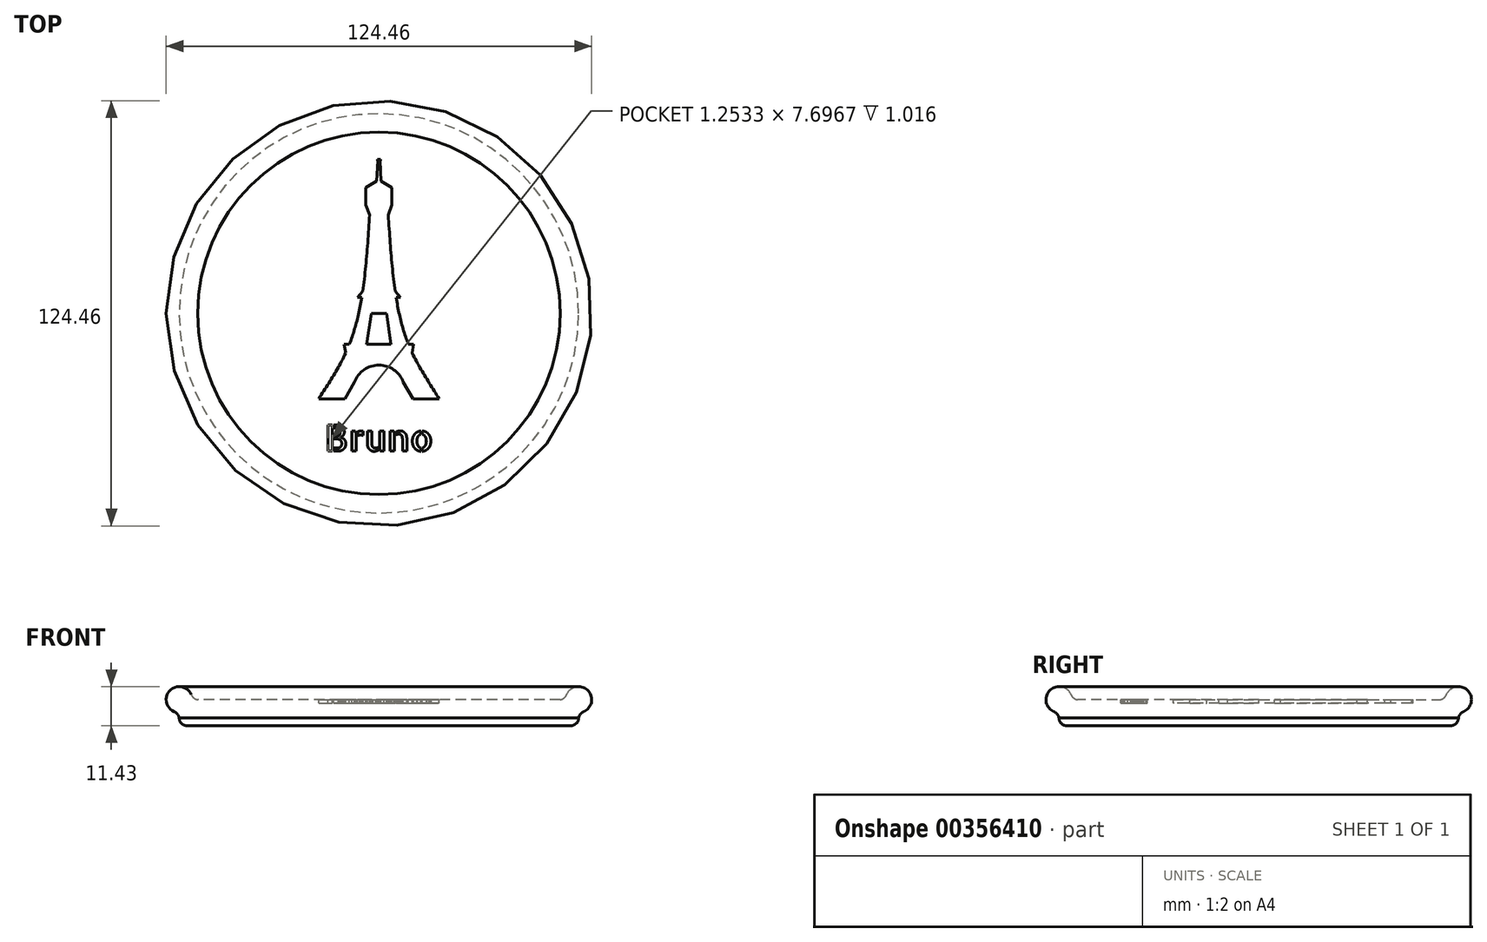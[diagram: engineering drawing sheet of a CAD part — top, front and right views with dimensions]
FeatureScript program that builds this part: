
annotation { "Feature Type Name" : "Feature", "Feature Type Description" : "" }
export const myFeature = defineFeature(function(context is Context, id is Id, definition is map)
    precondition{}
    {
        {
            var Q0;
            Q0=qCreatedBy(makeId("Top.planeOp"),FACE);
            var sketch = newSketch(context, id + "F0", { "sketchPlane" : qUnion([Q0])});
            skCircle(sketch, "E0", {"center": v(0, 0) * mm, "radius": 58.42 * mm});
            skSolve(sketch);
        }
        {
            var Q0;
            Q0=makeQuery(id+"F0.imprint","IMPRINT",FACE,{"disambiguationData":[TD([[makeQuery(id+"F0.imprint","IMPRINT",EDGE,{"derivedFrom":sQuery(id+"F0.wireOp",EDGE,"E0")}),1.0]])]});
            extrude(context, id + "F1", {"entities" : qUnion([Q0]), "depth" : 7.62 * mm, "offsetDistance" : 25.4 * mm});
        }
        {
            var Q0;
            Q0=makeQuery(id+"F1.opExtrude","CAP_FACE",FACE,{"disambiguationData":[OSD([sQuery(id+"F0.wireOp",EDGE,"E0")])],"isStart":false});
            var sketch = newSketch(context, id + "F2", { "sketchPlane" : qUnion([Q0])});
            skLineSegment(sketch, "E1", {"start": v(0, 0) * mm, "end": v(-58.42, 0) * mm});
            skSolve(sketch);
        }
        {
            var Q0;
            Q0=sQuery(id+"F2.wireOp",EDGE,"E1");
            cPlane(context, id + "F3", {"entities" : qUnion([Q0]), "cplaneType" : CPlaneType.LINE_ANGLE, "offset" : 25.4 * mm, "angle" : 0 * degree, "width" : 152.4 * mm, "height" : 152.4 * mm});
        }
        {
            var Q0;
            Q0=qCreatedBy(id+"F3.planeOp",FACE);
            var sketch = newSketch(context, id + "F4", { "sketchPlane" : qUnion([Q0])});
            skCircle(sketch, "E2", {"center": v(-58.42, 7.62) * mm, "radius": 3.81 * mm});
            skLineSegment(sketch, "E3", {"start": v(-58.42, 7.62) * mm, "end": v(-54.9, 9.08) * mm});
            skLineSegment(sketch, "E4", {"start": v(-54.9, 9.08) * mm, "end": v(-61.94, 6.16) * mm});
            skLineSegment(sketch, "E5", {"start": v(-54.9, 9.08) * mm, "end": v(-54.3, 7.62) * mm});
            skArc(sketch, "E6", {"start": v(-54.9, 9.08) * mm, "mid": v(-54.16, 8.1) * mm, "end": v(-53.03, 7.62) * mm});
            skLineSegment(sketch, "E7", {"start": v(-54.3, 7.62) * mm, "end": v(-53.03, 7.62) * mm});
            skLineSegment(sketch, "E8", {"start": v(-58.42, 7.62) * mm, "end": v(-59.88, 4.1) * mm});
            skLineSegment(sketch, "E9", {"start": v(-59.88, 4.1) * mm, "end": v(-58.42, 3.5) * mm});
            skLineSegment(sketch, "E10", {"start": v(-58.42, 3.5) * mm, "end": v(-58.42, 2.23) * mm});
            skArc(sketch, "E11", {"start": v(-58.42, 2.23) * mm, "mid": v(-58.9, 3.36) * mm, "end": v(-59.88, 4.1) * mm});
            skLineSegment(sketch, "E12", {"start": v(-58.42, 3.5) * mm, "end": v(-58.42, 3.81) * mm});
            skLineSegment(sketch, "E13", {"start": v(-54.3, 7.62) * mm, "end": v(-54.6, 7.62) * mm});
            skSolve(sketch);
        }
        {
            var Q0;
            {var subQ0=sQuery(id+"F4.wireOp",EDGE,"E4");var subQ1=sQuery(id+"F4.wireOp",EDGE,"E2");var subQ3=makeQuery(id+"F4.imprint","INTERSECT",VERTEX,{"derivedFrom":[subQ1,subQ0]});Q0=makeQuery(id+"F4.imprint","IMPRINT",FACE,{"disambiguationData":[TD([[makeQuery(id+"F4.imprint","IMPRINT",EDGE,{"disambiguationData":[TD([[subQ3,1.0]])],"derivedFrom":subQ0}),-1.0]])]});}
            var Q1;
            {var subQ3=sQuery(id+"F4.wireOp",EDGE,"E8");Q1=makeQuery(id+"F4.imprint","IMPRINT",FACE,{"disambiguationData":[TD([[makeQuery(id+"F4.imprint","IMPRINT",EDGE,{"derivedFrom":subQ3}),-1.0]])]});}
            var Q2;
            {var subQ3=sQuery(id+"F4.wireOp",EDGE,"E8");Q2=makeQuery(id+"F4.imprint","IMPRINT",FACE,{"disambiguationData":[TD([[makeQuery(id+"F4.imprint","IMPRINT",EDGE,{"derivedFrom":subQ3}),1.0]])]});}
            var Q3;
            {var subQ0=sQuery(id+"F4.wireOp",EDGE,"E5");Q3=makeQuery(id+"F4.imprint","IMPRINT",FACE,{"disambiguationData":[TD([[makeQuery(id+"F4.imprint","IMPRINT",EDGE,{"derivedFrom":subQ0}),-1.0]])]});}
            var Q4;
            Q4=makeQuery(id+"F4.imprint","IMPRINT",FACE,{"disambiguationData":[TD([[makeQuery(id+"F4.imprint","IMPRINT",EDGE,{"derivedFrom":sQuery(id+"F4.wireOp",EDGE,"E5")}),1.0]])]});
            var Q5;
            Q5=makeQuery(id+"F4.imprint","IMPRINT",FACE,{"disambiguationData":[TD([[makeQuery(id+"F4.imprint","IMPRINT",EDGE,{"derivedFrom":sQuery(id+"F4.wireOp",EDGE,"E9")}),-1.0]])]});
            var Q6;
            {var subQ0=sQuery(id+"F4.wireOp",EDGE,"E9");Q6=makeQuery(id+"F4.imprint","IMPRINT",FACE,{"disambiguationData":[TD([[makeQuery(id+"F4.imprint","IMPRINT",EDGE,{"derivedFrom":subQ0}),1.0]])]});}
            var Q7;
            Q7=makeQuery(id+"F1.opExtrude","CAP_EDGE",EDGE,{"disambiguationData":[OSD([sQuery(id+"F0.wireOp",EDGE,"E0")])],"isStart":false});
            revolve(context, id + "F5", {"operationType" : NewBodyOperationType.ADD, "surfaceOperationType" : NewSurfaceOperationType.NEW, "entities" : qUnion([Q0, Q1, Q2, Q3, Q4, Q5, Q6]), "axis" : qUnion([Q7]), "revolveType" : RevolveType.FULL});
        }
        {
            var Q0;
            Q0=makeQuery(id+"F1.opExtrude","CAP_EDGE",EDGE,{"disambiguationData":[OSD([sQuery(id+"F0.wireOp",EDGE,"E0")])],"isStart":true});
            fillet(context, id + "F6", {"entities" : qUnion([Q0]), "radius" : 2.3 * mm, "tangentPropagation" : true, "allowEdgeOverflow" : false});
        }
        {
            var Q0;
            Q0=makeQuery(id+"F1.opExtrude","CAP_FACE",FACE,{"disambiguationData":[OSD([sQuery(id+"F0.wireOp",EDGE,"E0")])],"isStart":false});
            var sketch = newSketch(context, id + "F7", { "sketchPlane" : qUnion([Q0])});
            skPoint(sketch, "E14", {"position": v(-17.61, -25.03) * mm});
            skPoint(sketch, "E15", {"position": v(-9.36, -10.73) * mm});
            skPoint(sketch, "E16", {"position": v(-4.75, 6.45) * mm});
            skPoint(sketch, "E17", {"position": v(-2.54, 31.75) * mm});
            skPoint(sketch, "E18", {"position": v(2.54, 31.75) * mm});
            skPoint(sketch, "E19", {"position": v(4.75, 6.45) * mm});
            skPoint(sketch, "E20", {"position": v(9.36, -10.73) * mm});
            skPoint(sketch, "E21", {"position": v(17.61, -25.03) * mm});
            skLineSegment(sketch, "E22", {"start": v(-2.54, 31.75) * mm, "end": v(2.54, 31.75) * mm});
            skLineSegment(sketch, "E23", {"start": v(4.75, 6.45) * mm, "end": v(2.54, 31.75) * mm});
            skLineSegment(sketch, "E24", {"start": v(4.75, 6.45) * mm, "end": v(9.36, -10.73) * mm});
            skLineSegment(sketch, "E25", {"start": v(9.36, -10.73) * mm, "end": v(17.61, -25.03) * mm});
            skLineSegment(sketch, "E26", {"start": v(-2.54, 31.75) * mm, "end": v(-4.75, 6.45) * mm});
            skLineSegment(sketch, "E27", {"start": v(-4.75, 6.45) * mm, "end": v(-9.36, -10.73) * mm});
            skLineSegment(sketch, "E28", {"start": v(-9.36, -10.73) * mm, "end": v(-17.61, -25.03) * mm});
            skPoint(sketch, "E29", {"position": v(0, 31.75) * mm});
            skLineSegment(sketch, "E30", {"start": v(-17.61, -25.03) * mm, "end": v(-10, -25.03) * mm});
            skLineSegment(sketch, "E31", {"start": v(17.61, -25.03) * mm, "end": v(10, -25.03) * mm});
            skLineSegment(sketch, "E32", {"start": v(-10, -25.03) * mm, "end": v(-4.28, -15.13) * mm});
            skLineSegment(sketch, "E33", {"start": v(-4.28, -15.13) * mm, "end": v(4.28, -15.13) * mm});
            skLineSegment(sketch, "E34", {"start": v(4.28, -15.13) * mm, "end": v(10, -25.03) * mm});
            skPoint(sketch, "E35", {"position": v(0, -15.13) * mm});
            skArc(sketch, "E36", {"start": v(7.13, -20.08) * mm, "mid": v(0, -15.13) * mm, "end": v(-7.13, -20.08) * mm});
            skFitSpline(sketch, "E37", {"points": [v(-17.61, -25.03) * mm, v(-9.36, -10.73) * mm, v(-4.75, 6.45) * mm, v(-2.54, 31.75) * mm], "startDerivative": vector(29.5, 45.64) * mm, "endDerivative": vector(4.2, 70.25) * mm});
            skFitSpline(sketch, "E38", {"points": [v(2.54, 31.75) * mm, v(4.75, 6.45) * mm, v(9.36, -10.73) * mm, v(17.61, -25.03) * mm], "startDerivative": vector(4.64, -70.22) * mm, "endDerivative": vector(28.16, -46.47) * mm});
            skLineSegment(sketch, "E39", {"start": v(-3.8, -10.62) * mm, "end": v(3.81, -10.62) * mm});
            skLineSegment(sketch, "E40", {"start": v(3.81, -10.62) * mm, "end": v(2.22, 0) * mm});
            skLineSegment(sketch, "E41", {"start": v(2.22, 0) * mm, "end": v(-2.22, 0) * mm});
            skLineSegment(sketch, "E42", {"start": v(-2.22, 0) * mm, "end": v(-3.8, -10.62) * mm});
            skLineSegment(sketch, "E43", {"start": v(0, 0) * mm, "end": v(0, 31.75) * mm});
            skLineSegment(sketch, "E44", {"start": v(-9.36, -10.73) * mm, "end": v(-10.14, -9.03) * mm});
            skLineSegment(sketch, "E45", {"start": v(-10.14, -9.03) * mm, "end": v(10.14, -9.03) * mm});
            skLineSegment(sketch, "E46", {"start": v(10.14, -9.03) * mm, "end": v(9.36, -10.73) * mm});
            skLineSegment(sketch, "E47", {"start": v(-10.14, -9.03) * mm, "end": v(-9.75, -11.6) * mm});
            skPoint(sketch, "E47.endSnap0", {"position": v(-9.75, -9.88) * mm});
            skLineSegment(sketch, "E48", {"start": v(-9.75, -11.6) * mm, "end": v(9.76, -11.6) * mm});
            skLineSegment(sketch, "E49", {"start": v(9.76, -11.6) * mm, "end": v(10.14, -9.03) * mm});
            skLineSegment(sketch, "E50", {"start": v(-4.75, 6.45) * mm, "end": v(-6.25, 4.67) * mm});
            skLineSegment(sketch, "E51", {"start": v(-6.25, 4.67) * mm, "end": v(6.25, 4.67) * mm});
            skLineSegment(sketch, "E52", {"start": v(6.25, 4.67) * mm, "end": v(4.75, 6.45) * mm});
            skLineSegment(sketch, "E53", {"start": v(-0.64, 38.66) * mm, "end": v(-0.32, 44.72) * mm});
            skLineSegment(sketch, "E54", {"start": v(-0.32, 44.72) * mm, "end": v(0.32, 44.72) * mm});
            skLineSegment(sketch, "E55", {"start": v(0.32, 44.72) * mm, "end": v(0.63, 38.66) * mm});
            skLineSegment(sketch, "E56", {"start": v(-3.81, 31.75) * mm, "end": v(3.8, 31.75) * mm});
            skLineSegment(sketch, "E57", {"start": v(0.63, 38.66) * mm, "end": v(-0.64, 38.66) * mm});
            skPoint(sketch, "E58", {"position": v(0, -10.62) * mm});
            skPoint(sketch, "E59", {"position": v(0, 0) * mm});
            skLineSegment(sketch, "E60", {"start": v(-3.81, 31.75) * mm, "end": v(-2.72, 28.8) * mm});
            skLineSegment(sketch, "E61", {"start": v(2.73, 28.79) * mm, "end": v(3.8, 31.75) * mm});
            skLineSegment(sketch, "E62", {"start": v(-3.81, 31.75) * mm, "end": v(-3.81, 36.83) * mm});
            skLineSegment(sketch, "E63", {"start": v(-3.81, 36.83) * mm, "end": v(3.8, 36.83) * mm});
            skLineSegment(sketch, "E64", {"start": v(3.8, 36.83) * mm, "end": v(3.8, 31.75) * mm});
            skLineSegment(sketch, "E65", {"start": v(-3.81, 36.83) * mm, "end": v(-0.64, 38.66) * mm});
            skLineSegment(sketch, "E66", {"start": v(-0.64, 38.66) * mm, "end": v(0.63, 38.66) * mm});
            skLineSegment(sketch, "E67", {"start": v(0.63, 38.66) * mm, "end": v(3.8, 36.83) * mm});
            skLineSegment(sketch, "E68", {"start": v(-0.32, 44.72) * mm, "end": v(-0.44, 44.72) * mm});
            skLineSegment(sketch, "E69", {"start": v(-0.44, 44.72) * mm, "end": v(-0.44, 45.1) * mm});
            skLineSegment(sketch, "E70", {"start": v(-0.44, 45.1) * mm, "end": v(0.44, 45.1) * mm});
            skLineSegment(sketch, "E71", {"start": v(0.44, 45.1) * mm, "end": v(0.44, 44.72) * mm});
            skLineSegment(sketch, "E72", {"start": v(0.44, 44.72) * mm, "end": v(0.32, 44.72) * mm});
            skSolve(sketch);
        }
        {
            var Q0;
            {var subQ10=sQuery(id+"F7.wireOp",EDGE,"E30");Q0=makeQuery(id+"F7.imprint","IMPRINT",FACE,{"disambiguationData":[TD([[makeQuery(id+"F7.imprint","IMPRINT",EDGE,{"derivedFrom":subQ10}),1.0]])]});}
            var Q1;
            {var subQ0=sQuery(id+"F7.wireOp",EDGE,"E33");var subQ1=sQuery(id+"F7.wireOp",EDGE,"E32");var subQ2=makeQuery(id+"F7.imprint","INTERSECT",VERTEX,{"derivedFrom":[subQ1,subQ0]});Q1=makeQuery(id+"F7.imprint","IMPRINT",FACE,{"disambiguationData":[TD([[makeQuery(id+"F7.imprint","IMPRINT",EDGE,{"disambiguationData":[TD([[subQ2,1.0]])],"derivedFrom":subQ1}),-1.0]])]});}
            var Q2;
            {var subQ0=sQuery(id+"F7.wireOp",EDGE,"E34");var subQ1=sQuery(id+"F7.wireOp",EDGE,"E33");var subQ2=makeQuery(id+"F7.imprint","INTERSECT",VERTEX,{"derivedFrom":[subQ1,subQ0]});Q2=makeQuery(id+"F7.imprint","IMPRINT",FACE,{"disambiguationData":[TD([[makeQuery(id+"F7.imprint","IMPRINT",EDGE,{"disambiguationData":[TD([[subQ2,1.0]])],"derivedFrom":subQ1}),-1.0]])]});}
            var Q3;
            {var subQ8=sQuery(id+"F7.wireOp",EDGE,"E39");Q3=makeQuery(id+"F7.imprint","IMPRINT",FACE,{"disambiguationData":[TD([[makeQuery(id+"F7.imprint","IMPRINT",EDGE,{"derivedFrom":subQ8}),-1.0]])]});}
            var Q4;
            {var subQ0=sQuery(id+"F7.wireOp",EDGE,"E44");Q4=makeQuery(id+"F7.imprint","IMPRINT",FACE,{"disambiguationData":[TD([[makeQuery(id+"F7.imprint","IMPRINT",EDGE,{"derivedFrom":subQ0}),-1.0]])]});}
            var Q5;
            {var subQ0=sQuery(id+"F7.wireOp",EDGE,"E44");Q5=makeQuery(id+"F7.imprint","IMPRINT",FACE,{"disambiguationData":[TD([[makeQuery(id+"F7.imprint","IMPRINT",EDGE,{"derivedFrom":subQ0}),1.0]])]});}
            var Q6;
            {var subQ1=sQuery(id+"F7.wireOp",EDGE,"E28");var subQ3=sQuery(id+"F7.wireOp",EDGE,"E47");var subQ4=makeQuery(id+"F7.imprint","INTERSECT",VERTEX,{"derivedFrom":[subQ1,subQ3]});Q6=makeQuery(id+"F7.imprint","IMPRINT",FACE,{"disambiguationData":[TD([[makeQuery(id+"F7.imprint","IMPRINT",EDGE,{"disambiguationData":[TD([[subQ4,-1.0]])],"derivedFrom":subQ3}),1.0]])]});}
            var Q7;
            {var subQ1=sQuery(id+"F7.wireOp",EDGE,"E27");var subQ3=sQuery(id+"F7.wireOp",EDGE,"E45");var subQ4=makeQuery(id+"F7.imprint","INTERSECT",VERTEX,{"derivedFrom":[subQ1,subQ3]});Q7=makeQuery(id+"F7.imprint","IMPRINT",FACE,{"disambiguationData":[TD([[makeQuery(id+"F7.imprint","IMPRINT",EDGE,{"disambiguationData":[TD([[subQ4,-1.0]])],"derivedFrom":subQ3}),-1.0]])]});}
            var Q8;
            {var subQ7=sQuery(id+"F7.wireOp",EDGE,"E45");var subQ9=sQuery(id+"F7.wireOp",EDGE,"E37");var subQ11=makeQuery(id+"F7.imprint","INTERSECT",VERTEX,{"derivedFrom":[subQ9,subQ7]});Q8=makeQuery(id+"F7.imprint","IMPRINT",FACE,{"disambiguationData":[TD([[makeQuery(id+"F7.imprint","IMPRINT",EDGE,{"disambiguationData":[TD([[subQ11,-1.0]])],"derivedFrom":subQ9}),-1.0]])]});}
            var Q9;
            {var subQ6=sQuery(id+"F7.wireOp",EDGE,"E38");var subQ9=sQuery(id+"F7.wireOp",EDGE,"E51");var subQ11=makeQuery(id+"F7.imprint","INTERSECT",VERTEX,{"derivedFrom":[subQ6,subQ9]});Q9=makeQuery(id+"F7.imprint","IMPRINT",FACE,{"disambiguationData":[TD([[makeQuery(id+"F7.imprint","IMPRINT",EDGE,{"disambiguationData":[TD([[subQ11,-1.0]])],"derivedFrom":subQ6}),-1.0]])]});}
            var Q10;
            {var subQ0=sQuery(id+"F7.wireOp",EDGE,"E46");Q10=makeQuery(id+"F7.imprint","IMPRINT",FACE,{"disambiguationData":[TD([[makeQuery(id+"F7.imprint","IMPRINT",EDGE,{"derivedFrom":subQ0}),1.0]])]});}
            var Q11;
            {var subQ1=sQuery(id+"F7.wireOp",EDGE,"E25");var subQ3=sQuery(id+"F7.wireOp",EDGE,"E49");var subQ4=makeQuery(id+"F7.imprint","INTERSECT",VERTEX,{"derivedFrom":[subQ1,subQ3]});Q11=makeQuery(id+"F7.imprint","IMPRINT",FACE,{"disambiguationData":[TD([[makeQuery(id+"F7.imprint","IMPRINT",EDGE,{"disambiguationData":[TD([[subQ4,1.0]])],"derivedFrom":subQ3}),1.0]])]});}
            var Q12;
            {var subQ0=sQuery(id+"F7.wireOp",EDGE,"E46");Q12=makeQuery(id+"F7.imprint","IMPRINT",FACE,{"disambiguationData":[TD([[makeQuery(id+"F7.imprint","IMPRINT",EDGE,{"derivedFrom":subQ0}),-1.0]])]});}
            var Q13;
            {var subQ1=sQuery(id+"F7.wireOp",EDGE,"E24");var subQ3=sQuery(id+"F7.wireOp",EDGE,"E45");var subQ4=makeQuery(id+"F7.imprint","INTERSECT",VERTEX,{"derivedFrom":[subQ1,subQ3]});Q13=makeQuery(id+"F7.imprint","IMPRINT",FACE,{"disambiguationData":[TD([[makeQuery(id+"F7.imprint","IMPRINT",EDGE,{"disambiguationData":[TD([[subQ4,1.0]])],"derivedFrom":subQ3}),-1.0]])]});}
            var Q14;
            {var subQ6=sQuery(id+"F7.wireOp",EDGE,"E43");var subQ8=sQuery(id+"F7.wireOp",EDGE,"E56");var subQ9=makeQuery(id+"F7.imprint","INTERSECT",VERTEX,{"derivedFrom":[subQ6,subQ8]});Q14=makeQuery(id+"F7.imprint","IMPRINT",FACE,{"disambiguationData":[TD([[makeQuery(id+"F7.imprint","IMPRINT",EDGE,{"disambiguationData":[TD([[subQ9,1.0]])],"derivedFrom":subQ6}),-1.0]])]});}
            var Q15;
            {var subQ0=sQuery(id+"F7.wireOp",EDGE,"E56");var subQ1=sQuery(id+"F7.wireOp",EDGE,"E43");var subQ2=makeQuery(id+"F7.imprint","INTERSECT",VERTEX,{"derivedFrom":[subQ1,subQ0]});Q15=makeQuery(id+"F7.imprint","IMPRINT",FACE,{"disambiguationData":[TD([[makeQuery(id+"F7.imprint","IMPRINT",EDGE,{"disambiguationData":[TD([[subQ2,1.0]])],"derivedFrom":subQ1}),1.0]])]});}
            var Q16;
            {var subQ0=sQuery(id+"F7.wireOp",EDGE,"E50");Q16=makeQuery(id+"F7.imprint","IMPRINT",FACE,{"disambiguationData":[TD([[makeQuery(id+"F7.imprint","IMPRINT",EDGE,{"derivedFrom":subQ0}),1.0]])]});}
            var Q17;
            {var subQ1=sQuery(id+"F7.wireOp",EDGE,"E27");var subQ3=sQuery(id+"F7.wireOp",EDGE,"E51");var subQ4=makeQuery(id+"F7.imprint","INTERSECT",VERTEX,{"derivedFrom":[subQ1,subQ3]});Q17=makeQuery(id+"F7.imprint","IMPRINT",FACE,{"disambiguationData":[TD([[makeQuery(id+"F7.imprint","IMPRINT",EDGE,{"disambiguationData":[TD([[subQ4,-1.0]])],"derivedFrom":subQ3}),1.0]])]});}
            var Q18;
            {var subQ0=sQuery(id+"F7.wireOp",EDGE,"E52");Q18=makeQuery(id+"F7.imprint","IMPRINT",FACE,{"disambiguationData":[TD([[makeQuery(id+"F7.imprint","IMPRINT",EDGE,{"derivedFrom":subQ0}),1.0]])]});}
            var Q19;
            {var subQ1=sQuery(id+"F7.wireOp",EDGE,"E24");var subQ3=sQuery(id+"F7.wireOp",EDGE,"E51");var subQ4=makeQuery(id+"F7.imprint","INTERSECT",VERTEX,{"derivedFrom":[subQ1,subQ3]});Q19=makeQuery(id+"F7.imprint","IMPRINT",FACE,{"disambiguationData":[TD([[makeQuery(id+"F7.imprint","IMPRINT",EDGE,{"disambiguationData":[TD([[subQ4,1.0]])],"derivedFrom":subQ3}),1.0]])]});}
            var Q20;
            {var subQ1=sQuery(id+"F7.wireOp",EDGE,"E26");var subQ3=sQuery(id+"F7.wireOp",EDGE,"E60");var subQ4=makeQuery(id+"F7.imprint","INTERSECT",VERTEX,{"derivedFrom":[subQ1,subQ3]});Q20=makeQuery(id+"F7.imprint","IMPRINT",FACE,{"disambiguationData":[TD([[makeQuery(id+"F7.imprint","IMPRINT",EDGE,{"disambiguationData":[TD([[subQ4,1.0]])],"derivedFrom":subQ1}),-1.0]])]});}
            var Q21;
            {var subQ0=sQuery(id+"F7.wireOp",EDGE,"E37");var subQ3=sQuery(id+"F7.wireOp",EDGE,"E60");var subQ5=makeQuery(id+"F7.imprint","INTERSECT",VERTEX,{"derivedFrom":[subQ0,subQ3]});Q21=makeQuery(id+"F7.imprint","IMPRINT",FACE,{"disambiguationData":[TD([[makeQuery(id+"F7.imprint","IMPRINT",EDGE,{"disambiguationData":[TD([[subQ5,1.0]])],"derivedFrom":subQ3}),1.0]])]});}
            var Q22;
            {var subQ1=sQuery(id+"F7.wireOp",EDGE,"E23");var subQ3=sQuery(id+"F7.wireOp",EDGE,"E61");var subQ4=makeQuery(id+"F7.imprint","INTERSECT",VERTEX,{"derivedFrom":[subQ1,subQ3]});Q22=makeQuery(id+"F7.imprint","IMPRINT",FACE,{"disambiguationData":[TD([[makeQuery(id+"F7.imprint","IMPRINT",EDGE,{"disambiguationData":[TD([[subQ4,-1.0]])],"derivedFrom":subQ1}),-1.0]])]});}
            var Q23;
            {var subQ0=sQuery(id+"F7.wireOp",EDGE,"E38");var subQ3=sQuery(id+"F7.wireOp",EDGE,"E61");var subQ5=makeQuery(id+"F7.imprint","INTERSECT",VERTEX,{"derivedFrom":[subQ0,subQ3]});Q23=makeQuery(id+"F7.imprint","IMPRINT",FACE,{"disambiguationData":[TD([[makeQuery(id+"F7.imprint","IMPRINT",EDGE,{"disambiguationData":[TD([[subQ5,-1.0]])],"derivedFrom":subQ3}),1.0]])]});}
            var Q24;
            {var subQ5=sQuery(id+"F7.wireOp",EDGE,"E62");Q24=makeQuery(id+"F7.imprint","IMPRINT",FACE,{"disambiguationData":[TD([[makeQuery(id+"F7.imprint","IMPRINT",EDGE,{"derivedFrom":subQ5}),-1.0]])]});}
            var Q25;
            Q25=makeQuery(id+"F7.imprint","IMPRINT",FACE,{"disambiguationData":[TD([[makeQuery(id+"F7.imprint","IMPRINT",EDGE,{"derivedFrom":sQuery(id+"F7.wireOp",EDGE,"E63")}),1.0]])]});
            var Q26;
            Q26=makeQuery(id+"F7.imprint","IMPRINT",FACE,{"disambiguationData":[TD([[makeQuery(id+"F7.imprint","IMPRINT",EDGE,{"derivedFrom":sQuery(id+"F7.wireOp",EDGE,"E53")}),-1.0]])]});
            var Q27;
            Q27=makeQuery(id+"F7.imprint","IMPRINT",FACE,{"disambiguationData":[TD([[makeQuery(id+"F7.imprint","IMPRINT",EDGE,{"derivedFrom":sQuery(id+"F7.wireOp",EDGE,"E54")}),1.0]])]});
            var Q28;
            {var subQ0=sQuery(id+"F7.wireOp",EDGE,"E39");Q28=makeQuery(id+"F7.imprint","IMPRINT",FACE,{"disambiguationData":[TD([[makeQuery(id+"F7.imprint","IMPRINT",EDGE,{"derivedFrom":subQ0}),1.0]])]});}
            extrude(context, id + "F8", {"entities" : qUnion([Q0, Q1, Q2, Q3, Q4, Q5, Q6, Q7, Q8, Q9, Q10, Q11, Q12, Q13, Q14, Q15, Q16, Q17, Q18, Q19, Q20, Q21, Q22, Q23, Q24, Q25, Q26, Q27, Q28]), "operationType" : NewBodyOperationType.REMOVE, "oppositeDirection" : true, "depth" : 1.02 * mm, "offsetDistance" : 25.4 * mm});
        }
        {
            var Q0;
            Q0=makeQuery(id+"F8.boolean.opBoolean","SPLIT",FACE,{"disambiguationData":[TD([makeQuery(id+"F5.opRevolve","SWEPT_FACE",FACE,{"disambiguationData":[OSD([sQuery(id+"F4.wireOp",EDGE,"E6")])]})])],"derivedFrom":makeQuery(id+"F1.opExtrude","CAP_FACE",FACE,{"disambiguationData":[OSD([sQuery(id+"F0.wireOp",EDGE,"E0")])],"isStart":false})});
            var sketch = newSketch(context, id + "F9", { "sketchPlane" : qUnion([Q0])});
            skText(sketch, "E73", { "text": "Bruno", "fontName": "AllertaStencil-Regular.ttf"});
            skLineSegment(sketch, "E74", {"start": v(0, -40.33) * mm, "end": v(0, -53.03) * mm});
            skLineSegment(sketch, "E75", {"start": v(0, -53.03) * mm, "end": v(0, -44.86) * mm});
            const initialGuessF9  = {"E73": [-0.01588, -0.04033, 1, 0, 0.0077]};
            skSetInitialGuess(sketch, initialGuessF9);
            skSolve(sketch);
        }
        {
            var Q0;
            Q0=makeQuery(id+"F9.imprint","IMPRINT",FACE,{"disambiguationData":[TD([[makeQuery(id+"F9.imprint","IMPRINT",EDGE,{"derivedFrom":sQuery(id+"F9.wireOp",EDGE,"E73.sketch_text.stroke-39")}),-1.0]])]});
            var Q1;
            Q1=makeQuery(id+"F9.imprint","IMPRINT",FACE,{"disambiguationData":[TD([[makeQuery(id+"F9.imprint","IMPRINT",EDGE,{"derivedFrom":sQuery(id+"F9.wireOp",EDGE,"E73.sketch_text.stroke-0")}),-1.0]])]});
            var Q2;
            Q2=makeQuery(id+"F9.imprint","IMPRINT",FACE,{"disambiguationData":[TD([[makeQuery(id+"F9.imprint","IMPRINT",EDGE,{"derivedFrom":sQuery(id+"F9.wireOp",EDGE,"E73.sketch_text.stroke-43")}),-1.0]])]});
            var Q3;
            Q3=makeQuery(id+"F9.imprint","IMPRINT",FACE,{"disambiguationData":[TD([[makeQuery(id+"F9.imprint","IMPRINT",EDGE,{"derivedFrom":sQuery(id+"F9.wireOp",EDGE,"E73.sketch_text.stroke-50")}),-1.0]])]});
            var Q4;
            Q4=makeQuery(id+"F9.imprint","IMPRINT",FACE,{"disambiguationData":[TD([[makeQuery(id+"F9.imprint","IMPRINT",EDGE,{"derivedFrom":sQuery(id+"F9.wireOp",EDGE,"E73.sketch_text.stroke-57")}),-1.0]])]});
            var Q5;
            Q5=makeQuery(id+"F9.imprint","IMPRINT",FACE,{"disambiguationData":[TD([[makeQuery(id+"F9.imprint","IMPRINT",EDGE,{"derivedFrom":sQuery(id+"F9.wireOp",EDGE,"E73.sketch_text.stroke-77")}),-1.0]])]});
            var Q6;
            Q6=makeQuery(id+"F9.imprint","IMPRINT",FACE,{"disambiguationData":[TD([[makeQuery(id+"F9.imprint","IMPRINT",EDGE,{"derivedFrom":sQuery(id+"F9.wireOp",EDGE,"E73.sketch_text.stroke-82")}),-1.0]])]});
            var Q7;
            Q7=makeQuery(id+"F9.imprint","IMPRINT",FACE,{"disambiguationData":[TD([[makeQuery(id+"F9.imprint","IMPRINT",EDGE,{"derivedFrom":sQuery(id+"F9.wireOp",EDGE,"E73.sketch_text.stroke-87")}),-1.0]])]});
            var Q8;
            Q8=makeQuery(id+"F9.imprint","IMPRINT",FACE,{"disambiguationData":[TD([[makeQuery(id+"F9.imprint","IMPRINT",EDGE,{"derivedFrom":sQuery(id+"F9.wireOp",EDGE,"E73.sketch_text.stroke-122")}),-1.0]])]});
            var Q9;
            Q9=makeQuery(id+"F9.imprint","IMPRINT",FACE,{"disambiguationData":[TD([[makeQuery(id+"F9.imprint","IMPRINT",EDGE,{"derivedFrom":sQuery(id+"F9.wireOp",EDGE,"E73.sketch_text.stroke-106")}),-1.0]])]});
            extrude(context, id + "F10", {"entities" : qUnion([Q0, Q1, Q2, Q3, Q4, Q5, Q6, Q7, Q8, Q9]), "operationType" : NewBodyOperationType.REMOVE, "oppositeDirection" : true, "depth" : 1.02 * mm, "offsetDistance" : 25.4 * mm});
        }
    });
